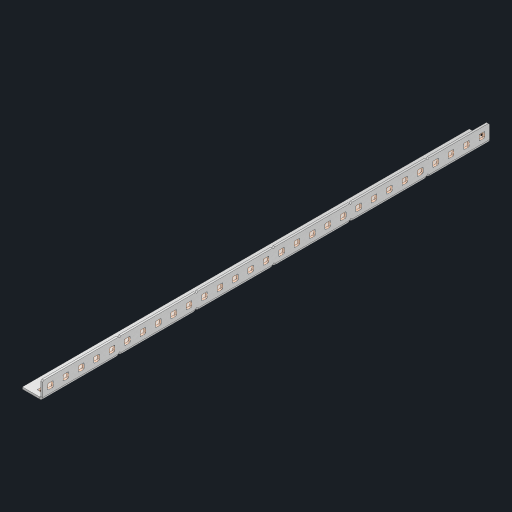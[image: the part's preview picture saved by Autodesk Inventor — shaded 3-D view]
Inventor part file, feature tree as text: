
AUTODESK INVENTOR PART (.ipt)
format: ipt  version: 2023 (Build 270158000, 158)  size: 941,568 bytes
history: native  units: in
note: dims shown in document units (in); Inventor stores cm internally (conversion verified against a paired STEP export)
features: other x63, extrude x57, sheet_metal_op x10, sketch x8, mirror x1, pattern_linear x1, chamfer x1
ambient origin geometry x8: Origin, YZ Plane, XZ Plane, XY Plane, X Axis, Y Axis, Z Axis, Center Point
bodies: Solid1 (feature_tree), Body (feature_tree)
feature tree (141):
  other  "Flange Pattern Plane"
  sheet_metal_op  "Flange Pattern"
  sheet_metal_op  "Body Pattern"
  other  "Arc Length"
  mirror  "Notch Mirror"
  pattern_linear  "Notch Pattern"  Spacing1=0.25in  [1 undecoded]
  chamfer  "End Chamfer"
  extrude  "Half Cut"  Depth=0.0625in
  sketch  "Sketch1"  dims[d0=1.5in]
  other  "Plate1"
  sketch  "Sketch2"  dims[d1=14.5in]
  other  "Plate2"
  sheet_metal_op  "Bend1"
  sheet_metal_op  "Corner1"
  sketch  "Sketch3"  dims[d2=0.0625in]
  other  "Flange Pattern Sketch"
  sketch  "Sketch7"  dims[d3=0.0625in]
  other  "Srf1"
  other  "Srf2"
  sketch  "Sketch8"  dims[d4=0.0312in]
  sketch  "Sketch9"  dims[d5=0.125in]
  other  "Srf91"
  sheet_metal_op  "Body Pattern Sketch"
  other  "Srf92"
  sketch  "Sketch13"  dims[d6=0.0625in]
  sketch  "Sketch14"  dims[d7=0.5in d8=90.0deg d9=0.0312in d10=0.25in d11=0.0625in d12=0.0625in d16=0.182in d17=0.02in d18=0.0625in d19=0.0in d20=0.25in d21=0.25in d46=0.172in d47=1.0in d48=0.0in d49=0.182in d50=0.02in d51=0.25in d52=0.25in d53=0.0625in d54=0.0in d55=0.172in d56=1.0in d57=0.0in d60=11.4173in d62=0.5in d63=0.3937in d65=0.5in d85=0.1473in d86=0.1782in d88=0.04in d89=0.0625in d90=0.0in d91=0.04in d92=0.0491in d95=2.5in d96=0.04in d97=0.25in d98=45.0deg d101=0.0in d102=2.497in d131=0.5in d132=11.4173in d134=0.5in d139=0.5in]
  other  "Srf856"
  other  "Srf1310"
  other  "Srf1311"
  other  "Srf1312"
  other  "Srf1376"
  other  "Srf1377"
  other  "Srf1728"
  other  "Srf1755"
  other  "Srf1878"
  other  "Srf1879"
  other  "Srf1880"
  other  "Srf1881"
  other  "Srf1882"
  other  "Srf1883"
  other  "Srf1884"
  other  "Srf1885"
  other  "Srf1886"
  other  "Srf1887"
  other  "Srf1888"
  other  "Srf1889"
  other  "Srf1890"
  other  "Srf1891"
  other  "Srf1892"
  other  "Srf1893"
  other  "Srf1894"
  other  "Srf1895"
  other  "Srf1896"
  other  "Srf1897"
  other  "Srf1898"
  other  "Srf1899"
  other  "Srf1900"
  other  "Srf1942"
  other  "Srf1943"
  other  "Srf1944"
  other  "Srf1945"
  other  "Srf1946"
  other  "Srf1947"
  other  "Srf1948"
  other  "Srf1949"
  other  "Srf1950"
  other  "Srf1951"
  other  "Srf1952"
  other  "Srf1953"
  other  "Srf1954"
  other  "Srf1955"
  other  "Srf1956"
  other  "Srf1957"
  other  "Srf1958"
  other  "Srf1959"
  other  "Srf1960"
  other  "Srf1961"
  other  "Srf1962"
  other  "Srf1963"
  other  "Srf1964"
  sheet_metal_op  "Flange Stamp"
  sheet_metal_op  "Flange Circle"
  sheet_metal_op  "Body Stamp"
  sheet_metal_op  "Body Circle"
  sheet_metal_op  "Notch"
  extrude  "ExtrusionSrf2"  Depth=0.0625in
  extrude  "ExtrusionSrf92"  Depth=0.5in
  extrude  "ExtrusionSrf856"  Depth=0.02in
  extrude  "ExtrusionSrf1310"  Depth=0.0625in
  extrude  "ExtrusionSrf1311"  TaperAngle=0.0deg  [1 undecoded]
  extrude  "ExtrusionSrf1312"  Depth=0.5in
  extrude  "ExtrusionSrf1376"  Depth=0.5in
  extrude  "ExtrusionSrf1377"  Depth=0.5in
  extrude  "ExtrusionSrf1728"  Depth=0.5in TaperAngle=0.0deg
  extrude  "ExtrusionSrf1755"  Depth=0.5in
  extrude  "ExtrusionSrf1878"  Depth=0.02in
  extrude  "ExtrusionSrf1879"  Depth=0.5in
  extrude  "ExtrusionSrf1880"  Depth=0.5in
  extrude  "ExtrusionSrf1881"  Depth=0.0625in
  extrude  "ExtrusionSrf1882"  TaperAngle=0.0deg  [1 undecoded]
  extrude  "ExtrusionSrf1883"  Depth=0.5in
  extrude  "ExtrusionSrf1884"  Depth=0.5in TaperAngle=0.0deg
  extrude  "ExtrusionSrf1885"  Depth=0.5in
  extrude  "ExtrusionSrf1886"  Depth=0.5in
  extrude  "ExtrusionSrf1887"  Depth=0.5in
  extrude  "ExtrusionSrf1888"  Depth=0.5in
  extrude  "ExtrusionSrf1889"  Depth=0.5in
  extrude  "ExtrusionSrf1890"  Depth=0.0625in
  extrude  "ExtrusionSrf1891"  TaperAngle=0.0deg  [1 undecoded]
  extrude  "ExtrusionSrf1892"  Depth=0.5in
  extrude  "ExtrusionSrf1893"  Depth=0.5in
  extrude  "ExtrusionSrf1894"  Depth=0.5in
  extrude  "ExtrusionSrf1895"  Depth=0.5in TaperAngle=45.0deg
  extrude  "ExtrusionSrf1896"  TaperAngle=0.0deg  [1 undecoded]
  extrude  "ExtrusionSrf1897"  Depth=0.5in
  extrude  "ExtrusionSrf1898"  Depth=0.5in
  extrude  "ExtrusionSrf1899"  Depth=0.5in
  extrude  "ExtrusionSrf1900"  Depth=0.5in
  extrude  "ExtrusionSrf1942"  Depth=0.5in
  extrude  "ExtrusionSrf1943"  [1 undecoded]
  extrude  "ExtrusionSrf1944"  [1 undecoded]
  extrude  "ExtrusionSrf1945"  [1 undecoded]
  extrude  "ExtrusionSrf1946"  [1 undecoded]
  extrude  "ExtrusionSrf1947"  [1 undecoded]
  extrude  "ExtrusionSrf1948"  [1 undecoded]
  extrude  "ExtrusionSrf1949"  [1 undecoded]
  extrude  "ExtrusionSrf1950"  [1 undecoded]
  extrude  "ExtrusionSrf1951"  [1 undecoded]
  extrude  "ExtrusionSrf1952"  [1 undecoded]
  extrude  "ExtrusionSrf1953"  [1 undecoded]
  extrude  "ExtrusionSrf1954"  [1 undecoded]
  extrude  "ExtrusionSrf1955"  [1 undecoded]
  extrude  "ExtrusionSrf1956"  [1 undecoded]
  extrude  "ExtrusionSrf1957"  [1 undecoded]
  extrude  "ExtrusionSrf1958"  [1 undecoded]
  extrude  "ExtrusionSrf1959"  [1 undecoded]
  extrude  "ExtrusionSrf1960"  [1 undecoded]
  extrude  "ExtrusionSrf1961"  [1 undecoded]
  extrude  "ExtrusionSrf1962"  [1 undecoded]
  extrude  "ExtrusionSrf1963"  [1 undecoded]
  extrude  "ExtrusionSrf1964"  [1 undecoded]
note: 27 required parameter values undecoded (feature->parameter linkage not recoverable at this tier; creation-order binding heuristic only, values carry confidence <= 0.55)
